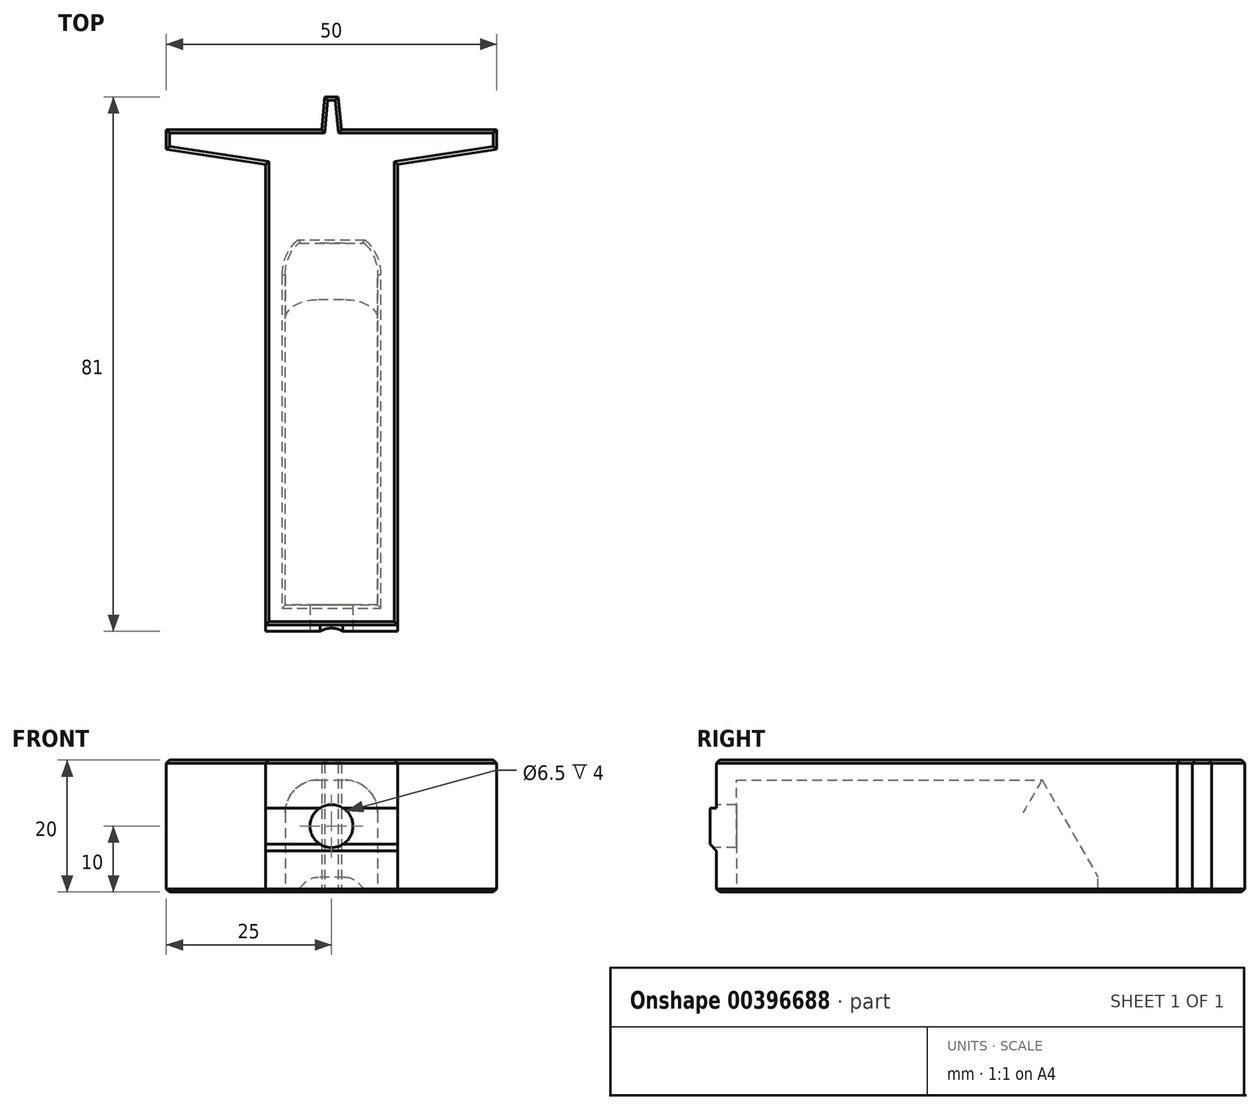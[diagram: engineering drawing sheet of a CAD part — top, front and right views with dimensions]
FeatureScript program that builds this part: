
annotation { "Feature Type Name" : "Feature", "Feature Type Description" : "" }
export const myFeature = defineFeature(function(context is Context, id is Id, definition is map)
    precondition{}
    {
        {
            var Q0;
            Q0=qCreatedBy(makeId("Top.planeOp"),FACE);
            var sketch = newSketch(context, id + "F0", { "sketchPlane" : qUnion([Q0])});
            skLineSegment(sketch, "E0.bottom", {"start": v(-10, 82.97) * mm, "end": v(10, 82.97) * mm});
            skLineSegment(sketch, "E0.top", {"start": v(-10, 7.97) * mm, "end": v(10, 7.97) * mm});
            skLineSegment(sketch, "E0.left", {"start": v(-10, 82.97) * mm, "end": v(-10, 7.97) * mm});
            skLineSegment(sketch, "E0.right", {"start": v(10, 82.97) * mm, "end": v(10, 7.97) * mm});
            skLineSegment(sketch, "E1", {"start": v(-25, 82.97) * mm, "end": v(-10, 82.97) * mm});
            skLineSegment(sketch, "E2", {"start": v(25, 82.97) * mm, "end": v(10, 82.97) * mm});
            skLineSegment(sketch, "E3", {"start": v(-1.5, 82.97) * mm, "end": v(-1, 87.97) * mm});
            skLineSegment(sketch, "E4", {"start": v(-1, 87.97) * mm, "end": v(1, 87.97) * mm});
            skLineSegment(sketch, "E5", {"start": v(1, 87.97) * mm, "end": v(1.5, 82.97) * mm});
            skLineSegment(sketch, "E6", {"start": v(-25, 82.97) * mm, "end": v(-25, 80) * mm});
            skLineSegment(sketch, "E7", {"start": v(-25, 80) * mm, "end": v(-10, 77.76) * mm});
            skLineSegment(sketch, "E8", {"start": v(10, 77.76) * mm, "end": v(25, 80) * mm});
            skLineSegment(sketch, "E9", {"start": v(25, 80) * mm, "end": v(25, 82.97) * mm});
            skSolve(sketch);
        }
        {
            var Q0;
            Q0 = qSketchRegion(id + "F0", true);
            extrude(context, id + "F1", {"entities" : qUnion([Q0]), "depth" : 20 * mm});
        }
        {
            var Q0;
            Q0=makeQuery(id+"F1.opExtrude","SWEPT_FACE",FACE,{"disambiguationData":[OSD([sQuery(id+"F0.wireOp",EDGE,"E0.top")])]});
            var sketch = newSketch(context, id + "F2", { "sketchPlane" : qUnion([Q0])});
            skLineSegment(sketch, "E10.bottom", {"start": v(-10, 12.75) * mm, "end": v(10, 12.75) * mm});
            skLineSegment(sketch, "E10.top", {"start": v(-10, 7.25) * mm, "end": v(10, 7.25) * mm});
            skLineSegment(sketch, "E10.left", {"start": v(-10, 12.75) * mm, "end": v(-10, 7.25) * mm});
            skLineSegment(sketch, "E10.right", {"start": v(10, 12.75) * mm, "end": v(10, 7.25) * mm});
            skSolve(sketch);
        }
        {
            var Q0;
            Q0=makeQuery(id+"F2.imprint","IMPRINT",FACE,{"disambiguationData":[TD([[makeQuery(id+"F2.imprint","IMPRINT",EDGE,{"derivedFrom":sQuery(id+"F2.wireOp",EDGE,"E10.bottom")}),-1.0]])]});
            extrude(context, id + "F3", {"entities" : qUnion([Q0]), "operationType" : NewBodyOperationType.ADD, "depth" : 1 * mm});
        }
        {
            var Q0;
            Q0=makeQuery(id+"F1.opExtrude","CAP_FACE",FACE,{"disambiguationData":[OSD([sQuery(id+"F0.wireOp",EDGE,"E0.bottom"),sQuery(id+"F0.wireOp",EDGE,"E0.top"),sQuery(id+"F0.wireOp",EDGE,"E0.left"),sQuery(id+"F0.wireOp",EDGE,"E0.right"),sQuery(id+"F0.wireOp",EDGE,"1AMYPGYv-ArdI-mm3B-GOt0-cCHU4pyTyYEb"),sQuery(id+"F0.wireOp",EDGE,"E1"),sQuery(id+"F0.wireOp",EDGE,"c4RxCUUY-6E3k-ZkMw-iAYc-6si8TpJcy46p"),sQuery(id+"F0.wireOp",EDGE,"E2"),sQuery(id+"F0.wireOp",EDGE,"E3"),sQuery(id+"F0.wireOp",EDGE,"E4"),sQuery(id+"F0.wireOp",EDGE,"E5")])],"isStart":true});
            var sketch = newSketch(context, id + "F4", { "sketchPlane" : qUnion([Q0])});
            skLineSegment(sketch, "E11.bottom", {"start": v(-7, -10.97) * mm, "end": v(7, -10.97) * mm});
            skLineSegment(sketch, "E11.top", {"start": v(-7, -65.76) * mm, "end": v(7, -65.76) * mm});
            skLineSegment(sketch, "E11.left", {"start": v(-7, -10.97) * mm, "end": v(-7, -65.76) * mm});
            skLineSegment(sketch, "E11.right", {"start": v(7, -10.97) * mm, "end": v(7, -65.76) * mm});
            skSolve(sketch);
        }
        {
            var Q0;
            Q0=makeQuery(id+"F4.imprint","IMPRINT",FACE,{"disambiguationData":[TD([[makeQuery(id+"F4.imprint","IMPRINT",EDGE,{"derivedFrom":sQuery(id+"F4.wireOp",EDGE,"E11.bottom")}),-1.0]])]});
            extrude(context, id + "F5", {"entities" : qUnion([Q0]), "operationType" : NewBodyOperationType.REMOVE, "oppositeDirection" : true, "depth" : 17 * mm});
        }
        {
            var Q0;
            Q0=makeQuery(id+"F3.opExtrude","CAP_FACE",FACE,{"disambiguationData":[OSD([sQuery(id+"F2.wireOp",EDGE,"E10.bottom"),sQuery(id+"F2.wireOp",EDGE,"E10.top"),sQuery(id+"F2.wireOp",EDGE,"E10.left"),sQuery(id+"F2.wireOp",EDGE,"E10.right")])],"isStart":false});
            var sketch = newSketch(context, id + "F6", { "sketchPlane" : qUnion([Q0])});
            skPoint(sketch, "E12", {"position": v(0, 10) * mm});
            skPoint(sketch, "E12.positionSnap0", {"position": v(-10, 10) * mm});
            skPoint(sketch, "E12.positionSnap1", {"position": v(0, 7.25) * mm});
            skSolve(sketch);
        }
        {
            var Q0;
            Q0=sQuery(id+"F6.wireOp",VERTEX,"E12");
            var Q1;
            Q1=makeQuery(id+"F1.opExtrude","SWEPT_BODY",BODY,{"disambiguationData":[OSD([sQuery(id+"F0.wireOp",EDGE,"E0.bottom"),sQuery(id+"F0.wireOp",EDGE,"E0.top"),sQuery(id+"F0.wireOp",EDGE,"E0.left"),sQuery(id+"F0.wireOp",EDGE,"E0.right"),sQuery(id+"F0.wireOp",EDGE,"1AMYPGYv-ArdI-mm3B-GOt0-cCHU4pyTyYEb"),sQuery(id+"F0.wireOp",EDGE,"E1"),sQuery(id+"F0.wireOp",EDGE,"c4RxCUUY-6E3k-ZkMw-iAYc-6si8TpJcy46p"),sQuery(id+"F0.wireOp",EDGE,"E2"),sQuery(id+"F0.wireOp",EDGE,"E3"),sQuery(id+"F0.wireOp",EDGE,"E4"),sQuery(id+"F0.wireOp",EDGE,"E5")])]});
            hole(context, id + "F7", {"style" : HoleStyle.C_BORE, "endStyle" : HoleEndStyle.BLIND, "holeDiameter" : 5.5 * mm, "cBoreDiameter" : 6.5 * mm, "cBoreDepth" : 5 * mm, "holeDepth" : 15 * mm, "isTappedThrough" : true, "tappedDepth" : 15 * mm, "tapClearance" : 0, "startFromSketch" : true, "locations" : qUnion([Q0]), "scope" : qUnion([Q1])});
        }
        {
            var Q0;
            Q0=makeQuery(id+"F5.boolean.opBoolean","COPY",EDGE,{"derivedFrom":makeQuery(id+"F5.opExtrude","CAP_EDGE",EDGE,{"disambiguationData":[OSD([sQuery(id+"F4.wireOp",EDGE,"E11.top")])],"isStart":true})});
            var Q1;
            Q1=makeQuery(id+"F5.boolean.opBoolean","COPY",EDGE,{"derivedFrom":makeQuery(id+"F5.opExtrude","CAP_EDGE",EDGE,{"disambiguationData":[OSD([sQuery(id+"F4.wireOp",EDGE,"E11.top")])],"isStart":false})});
            chamfer(context, id + "F8", {"entities" : qUnion([Q0, Q1]), "chamferType" : ChamferType.OFFSET_ANGLE, "width" : (17 / 2) * mm, "oppositeDirection" : false, "angle" : 60 * degree, "tangentPropagation" : true});
        }
        {
            var Q0;
            Q0=makeQuery(id+"F5.boolean.opBoolean","COPY",EDGE,{"derivedFrom":makeQuery(id+"F5.opExtrude","CAP_EDGE",EDGE,{"disambiguationData":[OSD([sQuery(id+"F4.wireOp",EDGE,"E11.right")])],"isStart":false})});
            var Q1;
            Q1=makeQuery(id+"F5.boolean.opBoolean","COPY",EDGE,{"derivedFrom":makeQuery(id+"F5.opExtrude","CAP_EDGE",EDGE,{"disambiguationData":[OSD([sQuery(id+"F4.wireOp",EDGE,"E11.left")])],"isStart":false})});
            var Q2;
            Q2=makeQuery(id+"F8.opChamfer","BLEND_EDGE",EDGE,{"blendedFrom":[makeQuery(id+"F5.boolean.opBoolean","COPY",EDGE,{"derivedFrom":makeQuery(id+"F5.opExtrude","CAP_EDGE",EDGE,{"disambiguationData":[OSD([sQuery(id+"F4.wireOp",EDGE,"E11.top")])],"isStart":false})}),makeQuery(id+"F5.boolean.opBoolean","COPY",FACE,{"derivedFrom":makeQuery(id+"F5.opExtrude","SWEPT_FACE",FACE,{"disambiguationData":[OSD([sQuery(id+"F4.wireOp",EDGE,"E11.left")])]})})],"blendedInto":[makeQuery(id+"F5.boolean.opBoolean","COPY",FACE,{"derivedFrom":makeQuery(id+"F5.opExtrude","SWEPT_FACE",FACE,{"disambiguationData":[OSD([sQuery(id+"F4.wireOp",EDGE,"E11.left")])]})})]});
            var Q3;
            Q3=makeQuery(id+"F8.opChamfer","BLEND_EDGE",EDGE,{"blendedFrom":[makeQuery(id+"F5.boolean.opBoolean","COPY",EDGE,{"derivedFrom":makeQuery(id+"F5.opExtrude","CAP_EDGE",EDGE,{"disambiguationData":[OSD([sQuery(id+"F4.wireOp",EDGE,"E11.top")])],"isStart":false})}),makeQuery(id+"F5.boolean.opBoolean","COPY",FACE,{"derivedFrom":makeQuery(id+"F5.opExtrude","SWEPT_FACE",FACE,{"disambiguationData":[OSD([sQuery(id+"F4.wireOp",EDGE,"E11.right")])]})})],"blendedInto":[makeQuery(id+"F5.boolean.opBoolean","COPY",FACE,{"derivedFrom":makeQuery(id+"F5.opExtrude","SWEPT_FACE",FACE,{"disambiguationData":[OSD([sQuery(id+"F4.wireOp",EDGE,"E11.right")])]})})]});
            fillet(context, id + "F9", {"entities" : qUnion([Q0, Q1, Q2, Q3]), "radius" : 5 * mm, "tangentPropagation" : true, "allowEdgeOverflow" : false});
        }
        {
            var Q0;
            Q0=makeQuery(id+"F1.opExtrude","CAP_FACE",FACE,{"disambiguationData":[OSD([sQuery(id+"F0.wireOp",EDGE,"E0.bottom"),sQuery(id+"F0.wireOp",EDGE,"E0.top"),sQuery(id+"F0.wireOp",EDGE,"E0.left"),sQuery(id+"F0.wireOp",EDGE,"E0.right"),sQuery(id+"F0.wireOp",EDGE,"E1"),sQuery(id+"F0.wireOp",EDGE,"E2"),sQuery(id+"F0.wireOp",EDGE,"E3"),sQuery(id+"F0.wireOp",EDGE,"E4"),sQuery(id+"F0.wireOp",EDGE,"E5"),sQuery(id+"F0.wireOp",EDGE,"E6"),sQuery(id+"F0.wireOp",EDGE,"E7"),sQuery(id+"F0.wireOp",EDGE,"E8"),sQuery(id+"F0.wireOp",EDGE,"E9")])],"isStart":false});
            var Q1;
            Q1=makeQuery(id+"F1.opExtrude","CAP_FACE",FACE,{"disambiguationData":[OSD([sQuery(id+"F0.wireOp",EDGE,"E0.bottom"),sQuery(id+"F0.wireOp",EDGE,"E0.top"),sQuery(id+"F0.wireOp",EDGE,"E0.left"),sQuery(id+"F0.wireOp",EDGE,"E0.right"),sQuery(id+"F0.wireOp",EDGE,"E1"),sQuery(id+"F0.wireOp",EDGE,"E2"),sQuery(id+"F0.wireOp",EDGE,"E3"),sQuery(id+"F0.wireOp",EDGE,"E4"),sQuery(id+"F0.wireOp",EDGE,"E5"),sQuery(id+"F0.wireOp",EDGE,"E6"),sQuery(id+"F0.wireOp",EDGE,"E7"),sQuery(id+"F0.wireOp",EDGE,"E8"),sQuery(id+"F0.wireOp",EDGE,"E9")])],"isStart":true});
            chamfer(context, id + "F10", {"entities" : qUnion([Q0, Q1]), "width" : .5 * mm, "tangentPropagation" : true});
        }
        {
            var Q0;
            {var subQ0=sQuery(id+"F2.wireOp",EDGE,"E10.bottom");Q0=makeQuery(id+"F7.hole-0.boolean.opBoolean","SPLIT",EDGE,{"disambiguationData":[TD([makeQuery(id+"F1.opExtrude","SWEPT_FACE",FACE,{"disambiguationData":[OSD([sQuery(id+"F0.wireOp",EDGE,"E0.right")])]})])],"derivedFrom":makeQuery(id+"F3.opExtrude","CAP_EDGE",EDGE,{"disambiguationData":[OSD([subQ0])],"isStart":true})});}
            var Q1;
            {var subQ0=sQuery(id+"F2.wireOp",EDGE,"E10.bottom");Q1=makeQuery(id+"F7.hole-0.boolean.opBoolean","SPLIT",EDGE,{"disambiguationData":[TD([makeQuery(id+"F1.opExtrude","SWEPT_FACE",FACE,{"disambiguationData":[OSD([sQuery(id+"F0.wireOp",EDGE,"E0.left")])]})])],"derivedFrom":makeQuery(id+"F3.opExtrude","CAP_EDGE",EDGE,{"disambiguationData":[OSD([subQ0])],"isStart":true})});}
            var Q2;
            {var subQ0=sQuery(id+"F2.wireOp",EDGE,"E10.top");Q2=makeQuery(id+"F7.hole-0.boolean.opBoolean","SPLIT",EDGE,{"disambiguationData":[TD([makeQuery(id+"F1.opExtrude","SWEPT_FACE",FACE,{"disambiguationData":[OSD([sQuery(id+"F0.wireOp",EDGE,"E0.right")])]})])],"derivedFrom":makeQuery(id+"F3.opExtrude","CAP_EDGE",EDGE,{"disambiguationData":[OSD([subQ0])],"isStart":true})});}
            var Q3;
            {var subQ0=sQuery(id+"F2.wireOp",EDGE,"E10.top");Q3=makeQuery(id+"F7.hole-0.boolean.opBoolean","SPLIT",EDGE,{"disambiguationData":[TD([makeQuery(id+"F1.opExtrude","SWEPT_FACE",FACE,{"disambiguationData":[OSD([sQuery(id+"F0.wireOp",EDGE,"E0.left")])]})])],"derivedFrom":makeQuery(id+"F3.opExtrude","CAP_EDGE",EDGE,{"disambiguationData":[OSD([subQ0])],"isStart":true})});}
            chamfer(context, id + "F11", {"entities" : qUnion([Q0, Q1, Q2, Q3]), "width" : 1 * mm, "tangentPropagation" : true});
        }
    });
